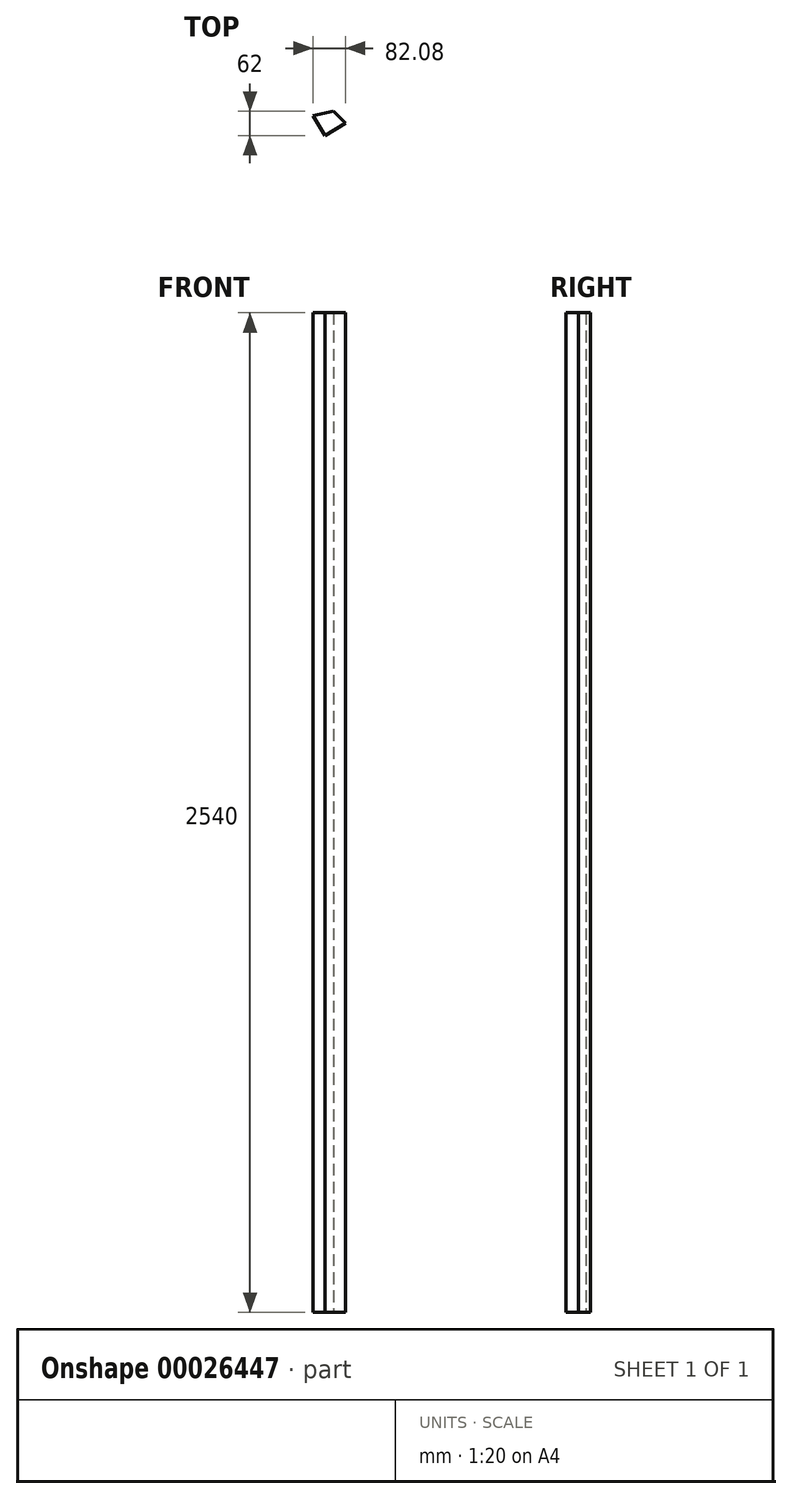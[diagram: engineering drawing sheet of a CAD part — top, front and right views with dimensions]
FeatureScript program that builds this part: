
annotation { "Feature Type Name" : "Feature", "Feature Type Description" : "" }
export const myFeature = defineFeature(function(context is Context, id is Id, definition is map)
    precondition{}
    {
        {
            var Q0;
            Q0=qCreatedBy(makeId("Top.planeOp"),FACE);
            var sketch = newSketch(context, id + "F0", { "sketchPlane" : qUnion([Q0])});
            skLineSegment(sketch, "E0", {"start": v(0, 0) * mm, "end": v(-51.75, -11.96) * mm});
            skLineSegment(sketch, "E1", {"start": v(-51.75, -11.96) * mm, "end": v(-21.78, -62) * mm});
            skLineSegment(sketch, "E2", {"start": v(-21.78, -62) * mm, "end": v(30.33, -30.78) * mm});
            skLineSegment(sketch, "E3", {"start": v(30.33, -30.78) * mm, "end": v(0, 0) * mm});
            skSolve(sketch);
        }
        {
            var Q0;
            Q0=makeQuery(id+"F0.imprint","IMPRINT",FACE,{"disambiguationData":[TD([[makeQuery(id+"F0.imprint","IMPRINT",EDGE,{"derivedFrom":sQuery(id+"F0.wireOp",EDGE,"E0")}),1.0]])]});
            extrude(context, id + "F1", {"entities" : qUnion([Q0]), "depth" : 2540 * mm});
        }
    });
